FCSTD DOCUMENT  (FreeCAD 1.0R39285 (Git))
Label: Sketch_refernceLotoV2
License: All rights reserved
LicenseURL: https://en.wikipedia.org/wiki/All_rights_reserved
objects: Sketcher::SketchObject×1, PartDesign::Body×1, App::Part×1, Image::ImagePlane×1
note: 3 computed .brp shape members not serialized (recipe doc carries the construction recipe); baked Part::Feature solids carry a one-line shape summary decoded from their .brp

FEATURE [Sketcher::SketchObject] Sketch
  ArcFitTolerance = 1e-06
  AttachmentSupport = -> [XY_Plane001]
  FullyConstrained = false
  MakeInternals = false
  MapMode = 5
  sketch-geometry (78):
    g0: LineSegment StartX=0 StartY=0 StartZ=0 EndX=-39 EndY=0 EndZ=0
    g1: LineSegment StartX=0 StartY=0 StartZ=0 EndX=0 EndY=30 EndZ=0
    g2: LineSegment [constr] StartX=0 StartY=30 StartZ=0 EndX=7 EndY=30 EndZ=0
    g3: LineSegment [constr] StartX=0 StartY=30 StartZ=0 EndX=0 EndY=38 EndZ=0
    g4: LineSegment [constr] StartX=0 StartY=38 StartZ=0 EndX=30 EndY=38 EndZ=0
    g5: LineSegment [constr] StartX=7 StartY=30 StartZ=0 EndX=30 EndY=38 EndZ=0
    g6: LineSegment [constr] StartX=7 StartY=30 StartZ=0 EndX=7 EndY=52 EndZ=0
    g7: LineSegment [constr] StartX=7 StartY=52 StartZ=0 EndX=30 EndY=38 EndZ=0
    g8: LineSegment [constr] StartX=7 StartY=52 StartZ=0 EndX=4 EndY=52 EndZ=0
    g9: LineSegment [constr] StartX=7 StartY=52 StartZ=0 EndX=10.5 EndY=52 EndZ=0
    g10: LineSegment [constr] StartX=10.5 StartY=52 StartZ=0 EndX=10.5 EndY=62 EndZ=0
    g11: LineSegment [constr] StartX=4 StartY=52 StartZ=0 EndX=10.5 EndY=62 EndZ=0
    g12: LineSegment [constr] StartX=10.5 StartY=62 StartZ=0 EndX=20.5 EndY=62 EndZ=0
    g13: LineSegment [constr] StartX=20.5 StartY=62 StartZ=0 EndX=20.5 EndY=87 EndZ=0
    g14: LineSegment [constr] StartX=10.5 StartY=62 StartZ=0 EndX=20.5 EndY=87 EndZ=0
    g15: LineSegment [constr] StartX=20.5 StartY=87 StartZ=0 EndX=5.5 EndY=87 EndZ=0
    g16: LineSegment [constr] StartX=5.5 StartY=87 StartZ=0 EndX=5.5 EndY=82 EndZ=0
    g17: LineSegment [constr] StartX=5.5 StartY=82 StartZ=0 EndX=20.5 EndY=87 EndZ=0
    g18: LineSegment [constr] StartX=5.5 StartY=82 StartZ=0 EndX=0.5 EndY=82 EndZ=0
    g19: LineSegment [constr] StartX=0.5 StartY=82 StartZ=0 EndX=0.5 EndY=79 EndZ=0
    g20: LineSegment [constr] StartX=0.5 StartY=79 StartZ=0 EndX=5.5 EndY=82 EndZ=0
    g21: LineSegment [constr] StartX=0.5 StartY=79 StartZ=0 EndX=-4.5 EndY=79 EndZ=0
    g22: LineSegment [constr] StartX=-4.5 StartY=79 StartZ=0 EndX=-4.5 EndY=89 EndZ=0
    g23: LineSegment [constr] StartX=0.5 StartY=79 StartZ=0 EndX=-4.5 EndY=89 EndZ=0
    g24: LineSegment [constr] StartX=-4.5 StartY=89 StartZ=0 EndX=-8.5 EndY=89 EndZ=0
    g25: LineSegment [constr] StartX=-8.5 StartY=89 StartZ=0 EndX=-8.5 EndY=104 EndZ=0
    g26: LineSegment [constr] StartX=-8.5 StartY=104 StartZ=0 EndX=-4.5 EndY=89 EndZ=0
    g27: LineSegment [constr] StartX=-8.5 StartY=104 StartZ=0 EndX=-18.5 EndY=104 EndZ=0
    g28: LineSegment [constr] StartX=-18.5 StartY=104 StartZ=0 EndX=-18.5 EndY=90 EndZ=0
    g29: LineSegment [constr] StartX=-18.5 StartY=90 StartZ=0 EndX=-8.5 EndY=104 EndZ=0
    g30: LineSegment [constr] StartX=-18.5 StartY=90 StartZ=0 EndX=-25 EndY=90 EndZ=0
    g31: LineSegment [constr] StartX=-25 StartY=90 StartZ=0 EndX=-25 EndY=93.5 EndZ=0
    g32: LineSegment [constr] StartX=-25 StartY=93.5 StartZ=0 EndX=-18.5 EndY=90 EndZ=0
    g33: LineSegment [constr] StartX=-25 StartY=93.5 StartZ=0 EndX=-25 EndY=108.5 EndZ=0
    g34: LineSegment [constr] StartX=-25 StartY=108.5 StartZ=0 EndX=-19 EndY=108.5 EndZ=0
    g35: LineSegment [constr] StartX=-19 StartY=108.5 StartZ=0 EndX=-25 EndY=93.5 EndZ=0
    g36: LineSegment [constr] StartX=-19 StartY=108.5 StartZ=0 EndX=-19 EndY=107.5 EndZ=0
    g37: LineSegment [constr] StartX=-19 StartY=107.5 StartZ=0 EndX=-28 EndY=107.5 EndZ=0
    g38: LineSegment [constr] StartX=-19 StartY=108.5 StartZ=0 EndX=-28 EndY=107.5 EndZ=0
    g39: LineSegment [constr] StartX=-28 StartY=107.5 StartZ=0 EndX=-28 EndY=116 EndZ=0
    g40: LineSegment [constr] StartX=-28 StartY=116 StartZ=0 EndX=-21 EndY=116 EndZ=0
    g41: LineSegment [constr] StartX=-28 StartY=107.5 StartZ=0 EndX=-21 EndY=116 EndZ=0
    g42: LineSegment [constr] StartX=-21 StartY=116 StartZ=0 EndX=14 EndY=116 EndZ=0
    g43: LineSegment [constr] StartX=14 StartY=116 StartZ=0 EndX=14 EndY=101 EndZ=0
    g44: LineSegment [constr] StartX=14 StartY=101 StartZ=0 EndX=-21 EndY=116 EndZ=0
    g45: LineSegment [constr] StartX=14 StartY=116 StartZ=0 EndX=14 EndY=136 EndZ=0
    g46: LineSegment [constr] StartX=14 StartY=136 StartZ=0 EndX=-7 EndY=136 EndZ=0
    g47: LineSegment [constr] StartX=-7 StartY=136 StartZ=0 EndX=-7 EndY=130.5 EndZ=0
    g48: LineSegment [constr] StartX=-7 StartY=130.5 StartZ=0 EndX=14 EndY=136 EndZ=0
    g49: LineSegment [constr] StartX=-7 StartY=130.5 StartZ=0 EndX=-36 EndY=130.5 EndZ=0
    g50: LineSegment [constr] StartX=-36 StartY=130.5 StartZ=0 EndX=-36 EndY=135 EndZ=0
    g51: LineSegment [constr] StartX=-36 StartY=135 StartZ=0 EndX=-7 EndY=130.5 EndZ=0
    g52: LineSegment StartX=0 StartY=30 StartZ=0 EndX=7 EndY=30 EndZ=0
    g53: ArcOfCircle CenterX=7.73497 CenterY=64.9495 CenterZ=0 NormalX=0 NormalY=0 NormalZ=1 AngleXU=0 Radius=34.9572 StartAngle=4.69136 EndAngle=5.40289
    g54: ArcOfCircle CenterX=39.1908 CenterY=66.0456 CenterZ=0 NormalX=0 NormalY=0 NormalZ=1 AngleXU=0 Radius=29.5132 StartAngle=3.93549 EndAngle=4.39571
    g55: ArcOfCircle CenterX=4.1426 CenterY=34.3593 CenterZ=0 NormalX=0 NormalY=0 NormalZ=1 AngleXU=0 Radius=17.8706 StartAngle=0.637801 EndAngle=1.41021
    g56: ArcOfCircle CenterX=7.17473 CenterY=53.7176 CenterZ=0 NormalX=0 NormalY=0 NormalZ=1 AngleXU=0 Radius=1.72643 StartAngle=2.59256 EndAngle=4.61101
    g57: ArcOfCircle CenterX=-3.17936 CenterY=65.6415 CenterZ=0 NormalX=0 NormalY=0 NormalZ=1 AngleXU=0 Radius=14.1558 StartAngle=5.39061 EndAngle=6.02301
    g58: ArcOfCircle CenterX=63.2286 CenterY=55.4086 CenterZ=0 NormalX=0 NormalY=0 NormalZ=1 AngleXU=0 Radius=53.139 StartAngle=2.50494 EndAngle=3.01723
    g59: ArcOfCircle CenterX=9.83975 CenterY=106.481 CenterZ=0 NormalX=0 NormalY=0 NormalZ=1 AngleXU=0 Radius=22.2068 StartAngle=4.85518 EndAngle=5.2131
    g60: ArcOfCircle CenterX=16.8385 CenterY=60.4844 CenterZ=0 NormalX=0 NormalY=0 NormalZ=1 AngleXU=0 Radius=24.3204 StartAngle=1.72929 EndAngle=2.0558
    g61: ArcOfCircle CenterX=10.3329 CenterY=70.2657 CenterZ=0 NormalX=0 NormalY=0 NormalZ=1 AngleXU=0 Radius=12.6906 StartAngle=1.96148 EndAngle=2.26095
    g62: ArcOfCircle CenterX=-0.804568 CenterY=83.9593 CenterZ=0 NormalX=0 NormalY=0 NormalZ=1 AngleXU=0 Radius=4.96161 StartAngle=5.12918 EndAngle=5.37644
    g63: ArcOfCircle CenterX=-18.832 CenterY=96.2657 CenterZ=0 NormalX=0 NormalY=0 NormalZ=1 AngleXU=0 Radius=6.27448 StartAngle=3.67157 EndAngle=4.76532
    g64: ArcOfCircle CenterX=-22.8254 CenterY=94.1631 CenterZ=0 NormalX=0 NormalY=0 NormalZ=1 AngleXU=0 Radius=1.77776 StartAngle=2.83598 EndAngle=3.78691
    g65: ArcOfCircle CenterX=-0.72341 CenterY=93.1842 CenterZ=0 NormalX=0 NormalY=0 NormalZ=1 AngleXU=0 Radius=23.8455 StartAngle=2.44411 EndAngle=3.07807
    g66: ArcOfCircle CenterX=-24.6427 CenterY=118.284 CenterZ=0 NormalX=0 NormalY=0 NormalZ=1 AngleXU=0 Radius=11.295 StartAngle=4.41059 EndAngle=5.2355
    g67: ArcOfCircle CenterX=-19.7979 CenterY=107.878 CenterZ=0 NormalX=0 NormalY=0 NormalZ=1 AngleXU=0 Radius=8.21083 StartAngle=1.71773 EndAngle=3.1876
    g68: ArcOfCircle CenterX=-19.1557 CenterY=71.97 CenterZ=0 NormalX=0 NormalY=0 NormalZ=1 AngleXU=0 Radius=44.0686 StartAngle=0.71915 EndAngle=1.61266
    g69: LineSegment [constr] StartX=-8.5 StartY=89 StartZ=0 EndX=-8.5 EndY=109 EndZ=0
    g70: ArcOfCircle CenterX=1.60279 CenterY=81.6332 CenterZ=0 NormalX=0 NormalY=0 NormalZ=1 AngleXU=0 Radius=2.2465 StartAngle=3.33335 EndAngle=4.53393
    g71: ArcOfCircle CenterX=-20.5639 CenterY=76.0962 CenterZ=0 NormalX=0 NormalY=0 NormalZ=1 AngleXU=0 Radius=20.6048 StartAngle=0.250559 EndAngle=0.676736
    g72: ArcOfCircle CenterX=19.5827 CenterY=104.217 CenterZ=0 NormalX=0 NormalY=0 NormalZ=1 AngleXU=0 Radius=28.4872 StartAngle=2.97288 EndAngle=3.7051
    g73: ArcOfCircle CenterX=-88.7525 CenterY=139.107 CenterZ=0 NormalX=0 NormalY=0 NormalZ=1 AngleXU=0 Radius=85.7138 StartAngle=5.67313 EndAngle=5.92428
    g74: ArcOfCircle CenterX=39.1755 CenterY=118.5 CenterZ=0 NormalX=0 NormalY=0 NormalZ=1 AngleXU=0 Radius=30.6604 StartAngle=2.53415 EndAngle=3.74904
    g75: ArcOfCircle CenterX=-10.6946 CenterY=187.448 CenterZ=0 NormalX=0 NormalY=0 NormalZ=1 AngleXU=0 Radius=57.0673 StartAngle=4.77718 EndAngle=5.15991
    g76: LineSegment [constr] StartX=-39 StartY=0 StartZ=0 EndX=-39 EndY=135 EndZ=0
    g77: ArcOfCircle CenterX=-8.91456 CenterY=232.913 CenterZ=0 NormalX=0 NormalY=0 NormalZ=1 AngleXU=0 Radius=102.431 StartAngle=4.41428 EndAngle=4.73108
  constraints (194):
    c: Distance(g0) = 39
    c: Coincident(g0,g-1)
    c: Horizontal(g0)
    c: Distance(g1) = 30
    c: Coincident(g1,g0)
    c: PointOnObject(g1,g-2)
    c: Distance(g2) = 7
    c: Coincident(g2,g1)
    c: Horizontal(g2)
    c: Distance(g3) = 8
    c: Coincident(g3,g1)
    c: PointOnObject(g3,g-2)
    c: Distance(g4) = 30
    c: Coincident(g4,g3)
    c: Horizontal(g4)
    c: Coincident(g5,g2)
    c: Coincident(g5,g4)
    c: Distance(g6) = 22
    c: Coincident(g6,g2)
    c: Vertical(g6)
    c: Coincident(g7,g6)
    c: Coincident(g7,g4)
    c: Distance(g8) = 3
    c: Coincident(g8,g6)
    c: Horizontal(g8)
    c: Distance(g9) = 3.5
    c: Coincident(g9,g6)
    c: Horizontal(g9)
    c: Distance(g10) = 10
    c: Coincident(g10,g9)
    c: Vertical(g10)
    c: Coincident(g11,g8)
    c: Coincident(g11,g10)
    c: Distance(g12) = 10
    c: Coincident(g12,g10)
    c: Horizontal(g12)
    c: Distance(g13) = 25
    c: Coincident(g13,g12)
    c: Vertical(g13)
    c: Coincident(g14,g10)
    c: Coincident(g14,g13)
    c: Distance(g15) = 15
    c: Coincident(g15,g13)
    c: Horizontal(g15)
    c: Distance(g16) = 5
    c: Coincident(g16,g15)
    c: Vertical(g16)
    c: Coincident(g17,g16)
    c: Coincident(g17,g13)
    c: Distance(g18) = 5
    c: Coincident(g18,g16)
    c: Horizontal(g18)
    c: Distance(g19) = 3
    c: Coincident(g19,g18)
    c: Vertical(g19)
    c: Coincident(g20,g19)
    c: Coincident(g20,g16)
    c: Distance(g21) = 5
    c: Coincident(g21,g19)
    c: Horizontal(g21)
    c: Distance(g22) = 10
    c: Coincident(g22,g21)
    c: Vertical(g22)
    c: Coincident(g23,g19)
    c: Coincident(g23,g22)
    c: Distance(g24) = 4
    c: Coincident(g24,g22)
    c: Horizontal(g24)
    c: Distance(g25) = 15
    c: Coincident(g25,g24)
    c: Vertical(g25)
    c: Coincident(g26,g25)
    c: Coincident(g26,g22)
    c: Distance(g27) = 10
    c: Coincident(g27,g25)
    c: Horizontal(g27)
    c: Distance(g28) = 14
    c: Coincident(g28,g27)
    c: Vertical(g28)
    c: Coincident(g29,g28)
    c: Coincident(g29,g25)
    c: Distance(g30) = 6.5
    c: Coincident(g30,g28)
    c: Horizontal(g30)
    c: Distance(g31) = 3.5
    c: Coincident(g31,g30)
    c: Vertical(g31)
    c: Coincident(g32,g31)
    c: Coincident(g32,g28)
    c: Distance(g33) = 15
    c: Coincident(g33,g31)
    c: Vertical(g33)
    c: Distance(g34) = 6
    c: Coincident(g34,g33)
    c: Horizontal(g34)
    c: Coincident(g35,g34)
    c: Coincident(g35,g31)
    c: Distance(g36) = 1
    c: Coincident(g36,g34)
    c: Vertical(g36)
    c: Distance(g37) = 9
    c: Coincident(g37,g36)
    c: Horizontal(g37)
    c: Coincident(g38,g34)
    c: Coincident(g38,g37)
    c: Distance(g39) = 8.5
    c: Coincident(g39,g37)
    c: Vertical(g39)
    c: Distance(g40) = 7
    c: Coincident(g40,g39)
    c: Horizontal(g40)
    c: Coincident(g41,g37)
    c: Coincident(g41,g40)
    c: Distance(g42) = 35
    c: Coincident(g42,g40)
    c: Horizontal(g42)
    c: Distance(g43) = 15
    c: Coincident(g43,g42)
    c: Vertical(g43)
    c: Coincident(g44,g43)
    c: Coincident(g44,g40)
    c: Distance(g45) = 20
    c: Coincident(g45,g42)
    c: Vertical(g45)
    c: Distance(g46) = 21
    c: Coincident(g46,g45)
    c: Horizontal(g46)
    c: Distance(g47) = 5.5
    c: Coincident(g47,g46)
    c: Vertical(g47)
    c: Coincident(g48,g47)
    c: Coincident(g48,g45)
    c: Distance(g49) = 29
    c: Coincident(g49,g47)
    c: Horizontal(g49)
    c: Distance(g50) = 4.5
    c: Coincident(g50,g49)
    c: Vertical(g50)
    c: Coincident(g51,g50)
    c: Coincident(g51,g47)
    c: Coincident(g52,g1)
    c: Coincident(g52,g2)
    c: Coincident(g53,g2)
    c: Coincident(g53,g4)
    c: Coincident(g54,g4)
    c: Symmetric(g7,g7,g54)
    c: Coincident(g55,g54)
    c: Coincident(g55,g6)
    c: Coincident(g56,g6)
    c: PointOnObject(g56,g11)
    c: Coincident(g57,g56)
    c: Coincident(g57,g10)
    c: Coincident(g58,g10)
    c: Coincident(g58,g13)
    c: Coincident(g59,g13)
    c: Symmetric(g17,g17,g59)
    c: Coincident(g60,g59)
    c: Coincident(g60,g16)
    c: Coincident(g61,g16)
    c: PointOnObject(g61,g20)
    c: PointOnObject(g62,g20)
    c: Coincident(g62,g61)
    c: Coincident(g63,g28)
    c: PointOnObject(g63,g32)
    c: Coincident(g64,g63)
    c: PointOnObject(g64,g35)
    c: Coincident(g65,g64)
    c: Coincident(g65,g34)
    c: Coincident(g66,g34)
    c: Coincident(g66,g37)
    c: Coincident(g67,g40)
    c: Coincident(g67,g37)
    c: Coincident(g68,g40)
    c: Coincident(g68,g43)
    c: Distance(g69) = 20
    c: Coincident(g69,g24)
    c: Vertical(g69)
    c: PointOnObject(g70,g23)
    c: Coincident(g70,g62)
    c: Coincident(g71,g70)
    c: Coincident(g71,g22)
    c: Coincident(g72,g22)
    c: Coincident(g72,g69)
    c: Coincident(g73,g28)
    c: Coincident(g73,g69)
    c: Coincident(g74,g45)
    c: Coincident(g74,g43)
    c: Coincident(g75,g47)
    c: Coincident(g75,g45)
    c: Distance(g76) = 135
    c: Coincident(g76,g0)
    c: Vertical(g76)
    c: Coincident(g77,g76)
    c: Coincident(g77,g47)
FEATURE [PartDesign::Body] Body  label="Cuerpo"
  AllowCompound = false
  Group = -> [Sketch]
  Origin = -> Origin001
FEATURE [App::Part] Part
  Group = -> [Body]
  Origin = -> Origin
FEATURE [Image::ImagePlane] Main_Board_Loto_V2_User_Drawings  label="Main_Board_Loto_V2-User_Drawings"
  XSize = 278.307
  YSize = 196.825
